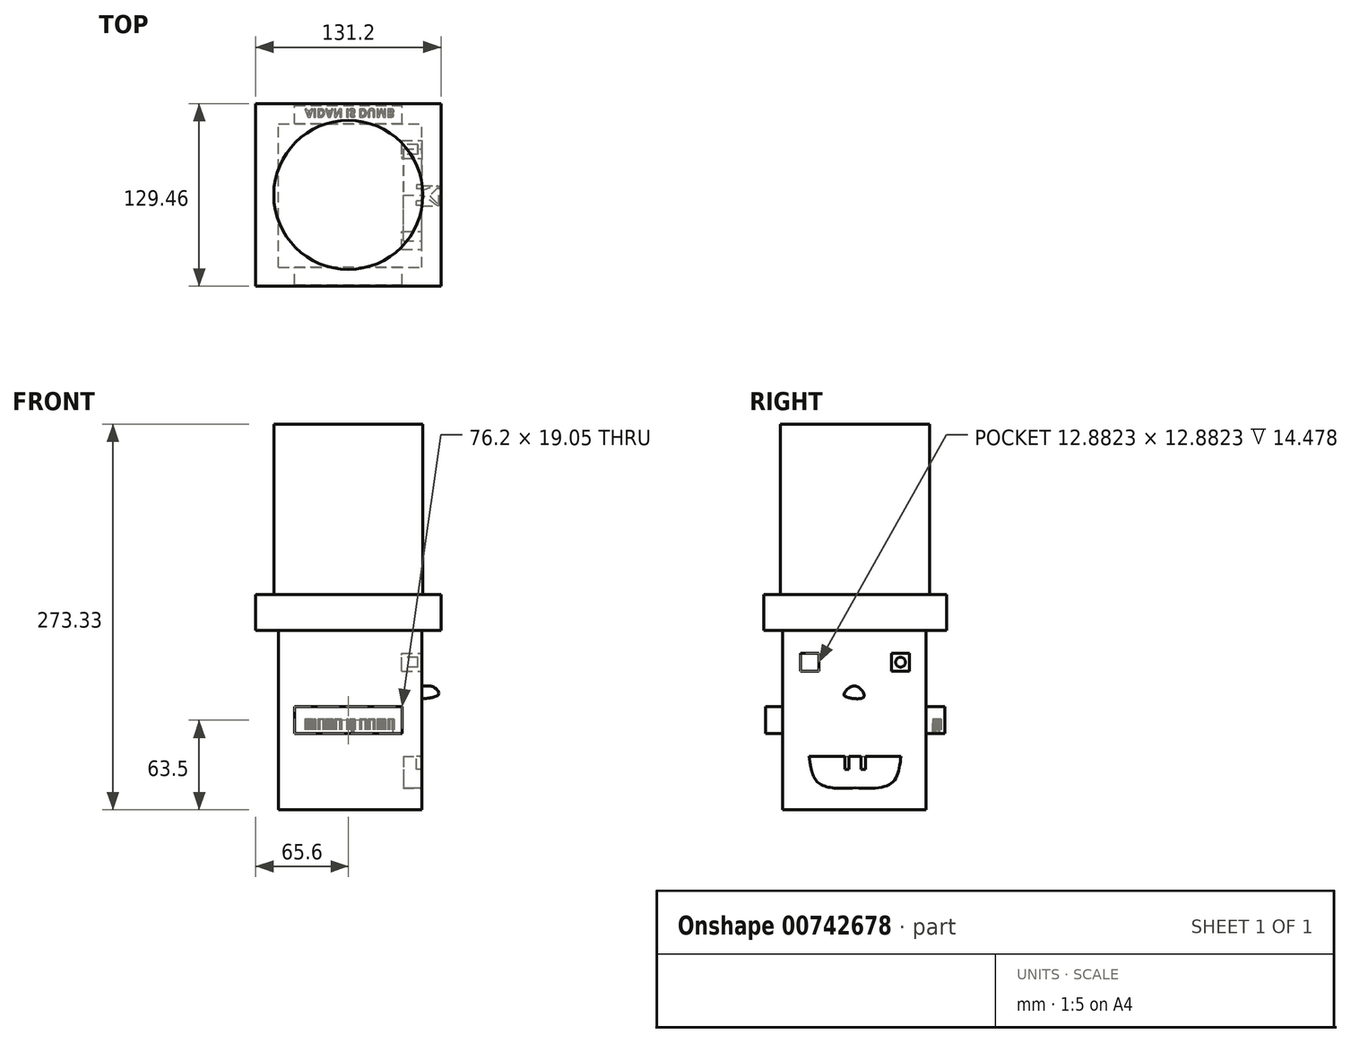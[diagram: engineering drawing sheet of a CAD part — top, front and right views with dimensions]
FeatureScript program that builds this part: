
annotation { "Feature Type Name" : "Feature", "Feature Type Description" : "" }
export const myFeature = defineFeature(function(context is Context, id is Id, definition is map)
    precondition{}
    {
        {
            var Q0;
            Q0=qCreatedBy(makeId("Front.planeOp"),FACE);
            var sketch = newSketch(context, id + "F0", { "sketchPlane" : qUnion([Q0])});
            skLineSegment(sketch, "E0.bottom", {"start": v(-38.1, -9.53) * mm, "end": v(38.1, -9.53) * mm});
            skLineSegment(sketch, "E0.top", {"start": v(-38.1, 9.53) * mm, "end": v(38.1, 9.53) * mm});
            skLineSegment(sketch, "E0.left", {"start": v(-38.1, -9.53) * mm, "end": v(-38.1, 9.53) * mm});
            skLineSegment(sketch, "E0.right", {"start": v(38.1, -9.53) * mm, "end": v(38.1, 9.53) * mm});
            skPoint(sketch, "E0.middle", {"position": v(0, 0) * mm});
            skLineSegment(sketch, "E1.bottom", {"start": v(69.87, 37.68) * mm, "end": v(98.1, 37.68) * mm});
            skLineSegment(sketch, "E1.top", {"start": v(69.87, 63.08) * mm, "end": v(98.1, 63.08) * mm});
            skLineSegment(sketch, "E1.left", {"start": v(69.87, 37.68) * mm, "end": v(69.87, 63.08) * mm});
            skLineSegment(sketch, "E1.right", {"start": v(98.1, 37.68) * mm, "end": v(98.1, 63.08) * mm});
            skPoint(sketch, "E1.middle", {"position": v(83.99, 50.38) * mm});
            skLineSegment(sketch, "E2", {"start": v(38.1, 9.52) * mm, "end": v(38.1, 38.1) * mm});
            skArc(sketch, "E3", {"start": v(38.1, 38.1) * mm, "mid": v(40.63, 43.9) * mm, "end": v(46.61, 45.99) * mm});
            skLineSegment(sketch, "E4", {"start": v(46.61, 45.99) * mm, "end": v(74.64, 45.99) * mm});
            skArc(sketch, "E5.0", {"start": v(28.2, 38.1) * mm, "mid": v(33.9, 51.17) * mm, "end": v(47.36, 55.87) * mm});
            skLineSegment(sketch, "E6", {"start": v(28.2, 38.1) * mm, "end": v(28.2, 9.52) * mm});
            skLineSegment(sketch, "E7", {"start": v(47.36, 55.87) * mm, "end": v(79, 55.87) * mm});
            skSolve(sketch);
        }
        {
            var Q0;
            Q0=makeQuery(id+"F0.imprint","IMPRINT",FACE,{"disambiguationData":[TD([[makeQuery(id+"F0.imprint","IMPRINT",EDGE,{"derivedFrom":sQuery(id+"F0.wireOp",EDGE,"E0.bottom")}),1.0]])]});
            extrude(context, id + "F1", {"entities" : qUnion([Q0]), "endBound" : BoundingType.SYMMETRIC, "depth" : 127 * mm, "offsetDistance" : 25.4 * mm});
        }
        {
            var Q0;
            Q0=qCreatedBy(makeId("Top.planeOp"),FACE);
            var sketch = newSketch(context, id + "F2", { "sketchPlane" : qUnion([Q0])});
            skLineSegment(sketch, "E8.bottom", {"start": v(-49.37, -51.34) * mm, "end": v(52.23, -51.34) * mm});
            skLineSegment(sketch, "E8.top", {"start": v(-49.37, 50.26) * mm, "end": v(52.23, 50.26) * mm});
            skLineSegment(sketch, "E8.left", {"start": v(-49.37, -51.34) * mm, "end": v(-49.37, 50.26) * mm});
            skLineSegment(sketch, "E8.right", {"start": v(52.23, -51.34) * mm, "end": v(52.23, 50.26) * mm});
            skSolve(sketch);
        }
        {
            var Q0;
            Q0=makeQuery(id+"F2.imprint","IMPRINT",FACE,{"disambiguationData":[TD([[makeQuery(id+"F2.imprint","IMPRINT",EDGE,{"derivedFrom":sQuery(id+"F2.wireOp",EDGE,"E8.bottom")}),1.0]])]});
            extrude(context, id + "F3", {"entities" : qUnion([Q0]), "operationType" : NewBodyOperationType.ADD, "endBound" : BoundingType.SYMMETRIC, "depth" : 127 * mm, "offsetDistance" : 25.4 * mm});
        }
        {
            var Q0;
            Q0=makeQuery(id+"F3.opExtrude","SWEPT_FACE",FACE,{"disambiguationData":[OSD([sQuery(id+"F2.wireOp",EDGE,"E8.right")])]});
            var sketch = newSketch(context, id + "F4", { "sketchPlane" : qUnion([Q0])});
            skLineSegment(sketch, "E9.bottom", {"start": v(-38.62, 34.67) * mm, "end": v(-25.74, 34.67) * mm});
            skLineSegment(sketch, "E9.top", {"start": v(-38.62, 47.55) * mm, "end": v(-25.74, 47.55) * mm});
            skLineSegment(sketch, "E9.left", {"start": v(-38.62, 34.67) * mm, "end": v(-38.62, 47.55) * mm});
            skLineSegment(sketch, "E9.right", {"start": v(-25.74, 34.67) * mm, "end": v(-25.74, 47.55) * mm});
            skPoint(sketch, "E9.middle", {"position": v(-32.18, 41.1) * mm});
            skPoint(sketch, "E10.MirrorP", {"position": v(32.18, 41.1) * mm});
            skLineSegment(sketch, "E11.MirrorCS", {"start": v(25.74, 34.67) * mm, "end": v(25.74, 47.55) * mm});
            skLineSegment(sketch, "E12.MirrorCS", {"start": v(38.62, 34.67) * mm, "end": v(25.74, 34.67) * mm});
            skLineSegment(sketch, "E13.MirrorCS", {"start": v(38.62, 34.67) * mm, "end": v(38.62, 47.55) * mm});
            skLineSegment(sketch, "E14.MirrorCS", {"start": v(38.62, 47.55) * mm, "end": v(25.74, 47.55) * mm});
            skSolve(sketch);
        }
        {
            var Q0;
            Q0 = qSketchRegion(id + "F4", true);
            extrude(context, id + "F5", {"entities" : qUnion([Q0]), "operationType" : NewBodyOperationType.REMOVE, "oppositeDirection" : true, "depth" : 14.48 * mm, "offsetDistance" : 25.4 * mm});
        }
        {
            var Q0;
            Q0=makeQuery(id+"F5.boolean.opBoolean","COPY",FACE,{"derivedFrom":makeQuery(id+"F5.opExtrude","CAP_FACE",FACE,{"disambiguationData":[OSD([sQuery(id+"F4.wireOp",EDGE,"E11.MirrorCS"),sQuery(id+"F4.wireOp",EDGE,"E12.MirrorCS"),sQuery(id+"F4.wireOp",EDGE,"E13.MirrorCS"),sQuery(id+"F4.wireOp",EDGE,"E14.MirrorCS")])],"isStart":false})});
            var sketch = newSketch(context, id + "F6", { "sketchPlane" : qUnion([Q0])});
            skCircle(sketch, "E15", {"center": v(32.18, 41.1) * mm, "radius": 3.5 * mm});
            skPoint(sketch, "E15.centerSnap0", {"position": v(32.18, 34.67) * mm});
            skPoint(sketch, "E15.centerSnap1", {"position": v(25.74, 41.1) * mm});
            skCircle(sketch, "E16.MirrorC", {"center": v(-32.18, 41.1) * mm, "radius": 3.5 * mm});
            skSolve(sketch);
        }
        {
            var Q0;
            Q0=makeQuery(id+"F6.imprint","IMPRINT",FACE,{"disambiguationData":[TD([[makeQuery(id+"F6.imprint","IMPRINT",EDGE,{"derivedFrom":sQuery(id+"F6.wireOp",EDGE,"E15")}),1.0]])]});
            var Q1;
            Q1=makeQuery(id+"F6.imprint","IMPRINT",FACE,{"disambiguationData":[TD([[makeQuery(id+"F6.imprint","IMPRINT",EDGE,{"derivedFrom":sQuery(id+"F6.wireOp",EDGE,"E16.MirrorC")}),-1.0]])]});
            extrude(context, id + "F7", {"entities" : qUnion([Q0, Q1]), "operationType" : NewBodyOperationType.ADD, "depth" : 11.43 * mm, "offsetDistance" : 25.4 * mm});
        }
        {
            var Q0;
            Q0=makeQuery(id+"F3.opExtrude","SWEPT_FACE",FACE,{"disambiguationData":[OSD([sQuery(id+"F2.wireOp",EDGE,"E8.right")])]});
            var sketch = newSketch(context, id + "F8", { "sketchPlane" : qUnion([Q0])});
            skFitSpline(sketch, "E17", {"points": [v(-32.56, -25.65) * mm, v(-25.87, -44.45) * mm, v(0, -47.95) * mm], "startDerivative": vector(6.38, -48.17) * mm, "endDerivative": vector(57.6, 2.43) * mm});
            skFitSpline(sketch, "E18", {"points": [v(-31.57, -33.14) * mm, v(-29.38, -39.75) * mm], "startDerivative": vector(2.13, -6.64) * mm, "endDerivative": vector(2.13, -6.64) * mm});
            skFitSpline(sketch, "E19.MirrorCS", {"points": [v(32.56, -25.65) * mm, v(25.87, -44.45) * mm, v(0, -47.95) * mm], "startDerivative": vector(-6.38, -48.17) * mm, "endDerivative": vector(-57.6, 2.43) * mm});
            skLineSegment(sketch, "E20", {"start": v(-32.56, -25.65) * mm, "end": v(32.56, -25.65) * mm});
            skSolve(sketch);
        }
        {
            var Q0;
            Q0 = qSketchRegion(id + "F8", true);
            extrude(context, id + "F9", {"entities" : qUnion([Q0]), "operationType" : NewBodyOperationType.REMOVE, "oppositeDirection" : true, "depth" : 13.2 * mm, "offsetDistance" : 25.4 * mm});
        }
        {
            var Q0;
            Q0=makeQuery(id+"F9.boolean.opBoolean","COPY",FACE,{"derivedFrom":makeQuery(id+"F9.opExtrude","SWEPT_FACE",FACE,{"disambiguationData":[OSD([sQuery(id+"F8.wireOp",EDGE,"E20")])]})});
            var sketch = newSketch(context, id + "F10", { "sketchPlane" : qUnion([Q0])});
            skLineSegment(sketch, "E21.bottom", {"start": v(52.23, -7.3) * mm, "end": v(48.24, -7.3) * mm});
            skLineSegment(sketch, "E21.top", {"start": v(52.23, -4.37) * mm, "end": v(48.24, -4.37) * mm});
            skLineSegment(sketch, "E21.left", {"start": v(52.23, -7.3) * mm, "end": v(52.23, -4.37) * mm});
            skLineSegment(sketch, "E21.right", {"start": v(48.24, -7.3) * mm, "end": v(48.24, -4.37) * mm});
            skLineSegment(sketch, "E22.MirrorCS", {"start": v(52.23, 4.37) * mm, "end": v(48.24, 4.37) * mm});
            skLineSegment(sketch, "E23.MirrorCS", {"start": v(52.23, 7.3) * mm, "end": v(48.24, 7.3) * mm});
            skLineSegment(sketch, "E24.MirrorCS", {"start": v(48.24, 7.3) * mm, "end": v(48.24, 4.37) * mm});
            skLineSegment(sketch, "E25.MirrorCS", {"start": v(52.23, 7.3) * mm, "end": v(52.23, 4.37) * mm});
            skSolve(sketch);
        }
        {
            var Q0;
            Q0=makeQuery(id+"F10.imprint","IMPRINT",FACE,{"disambiguationData":[TD([[makeQuery(id+"F10.imprint","IMPRINT",EDGE,{"derivedFrom":sQuery(id+"F10.wireOp",EDGE,"E23.MirrorCS")}),1.0]])]});
            var Q1;
            Q1=makeQuery(id+"F10.imprint","IMPRINT",FACE,{"disambiguationData":[TD([[makeQuery(id+"F10.imprint","IMPRINT",EDGE,{"derivedFrom":sQuery(id+"F10.wireOp",EDGE,"E21.bottom")}),-1.0]])]});
            extrude(context, id + "F11", {"entities" : qUnion([Q0, Q1]), "operationType" : NewBodyOperationType.ADD, "depth" : 9.16 * mm, "offsetDistance" : 25.4 * mm});
        }
        {
            var Q0;
            Q0=makeQuery(id+"F3.opExtrude","CAP_FACE",FACE,{"disambiguationData":[OSD([sQuery(id+"F2.wireOp",EDGE,"E8.bottom"),sQuery(id+"F2.wireOp",EDGE,"E8.top"),sQuery(id+"F2.wireOp",EDGE,"E8.left"),sQuery(id+"F2.wireOp",EDGE,"E8.right")])],"isStart":false});
            var sketch = newSketch(context, id + "F12", { "sketchPlane" : qUnion([Q0])});
            skLineSegment(sketch, "E26.bottom", {"start": v(65.6, -64.73) * mm, "end": v(-65.6, -64.73) * mm});
            skLineSegment(sketch, "E26.top", {"start": v(65.6, 64.73) * mm, "end": v(-65.6, 64.73) * mm});
            skLineSegment(sketch, "E26.left", {"start": v(65.6, -64.73) * mm, "end": v(65.6, 64.73) * mm});
            skLineSegment(sketch, "E26.right", {"start": v(-65.6, -64.73) * mm, "end": v(-65.6, 64.73) * mm});
            skPoint(sketch, "E26.middle", {"position": v(0, 0) * mm});
            skSolve(sketch);
        }
        {
            var Q0;
            Q0=makeQuery(id+"F12.imprint","IMPRINT",FACE,{"disambiguationData":[TD([[makeQuery(id+"F12.imprint","IMPRINT",EDGE,{"derivedFrom":sQuery(id+"F12.wireOp",EDGE,"E26.bottom")}),-1.0]])]});
            var Q1;
            Q1=makeQuery(id+"F12.imprint","IMPRINT",FACE,{"disambiguationData":[TD([[makeQuery(id+"F12.imprint","IMPRINT",EDGE,{"derivedFrom":makeQuery(id+"F3.opExtrude","CAP_EDGE",EDGE,{"disambiguationData":[OSD([sQuery(id+"F2.wireOp",EDGE,"E8.bottom")])],"isStart":false})}),1.0]])]});
            extrude(context, id + "F13", {"entities" : qUnion([Q0, Q1]), "operationType" : NewBodyOperationType.ADD, "depth" : 25.4 * mm, "offsetDistance" : 25.4 * mm});
        }
        {
            var Q0;
            Q0=makeQuery(id+"F13.opExtrude","CAP_FACE",FACE,{"disambiguationData":[OSD([sQuery(id+"F12.wireOp",EDGE,"E26.bottom"),sQuery(id+"F12.wireOp",EDGE,"E26.top"),sQuery(id+"F12.wireOp",EDGE,"E26.left"),sQuery(id+"F12.wireOp",EDGE,"E26.right")])],"isStart":false});
            var sketch = newSketch(context, id + "F14", { "sketchPlane" : qUnion([Q0])});
            skCircle(sketch, "E27", {"center": v(0, 0) * mm, "radius": 52.8 * mm});
            skSolve(sketch);
        }
        {
            var Q0;
            Q0=makeQuery(id+"F14.imprint","IMPRINT",FACE,{"disambiguationData":[TD([[makeQuery(id+"F14.imprint","IMPRINT",EDGE,{"derivedFrom":sQuery(id+"F14.wireOp",EDGE,"E27")}),1.0]])]});
            extrude(context, id + "F15", {"entities" : qUnion([Q0]), "operationType" : NewBodyOperationType.ADD, "depth" : 120.93 * mm, "offsetDistance" : 25.4 * mm});
        }
        {
            var Q0;
            Q0=makeQuery(id+"F11.boolean.opBoolean","MERGE",FACE,{"derivedFrom":[makeQuery(id+"F3.opExtrude","SWEPT_FACE",FACE,{"disambiguationData":[OSD([sQuery(id+"F2.wireOp",EDGE,"E8.right")])]}),makeQuery(id+"F11.opExtrude","SWEPT_FACE",FACE,{"disambiguationData":[OSD([sQuery(id+"F10.wireOp",EDGE,"E21.left")])]}),makeQuery(id+"F11.opExtrude","SWEPT_FACE",FACE,{"disambiguationData":[OSD([sQuery(id+"F10.wireOp",EDGE,"E25.MirrorCS")])]})]});
            var sketch = newSketch(context, id + "F16", { "sketchPlane" : qUnion([Q0])});
            skSolve(sketch);
        }
        {
            var Q0;
            {var subQ5=sQuery(id+"F2.wireOp",EDGE,"E8.right");Q0=makeQuery(id+"F16.imprint","IMPRINT",FACE,{"disambiguationData":[TD([[makeQuery(id+"F16.imprint","IMPRINT",EDGE,{"derivedFrom":makeQuery(id+"F3.opExtrude","CAP_EDGE",EDGE,{"disambiguationData":[OSD([subQ5])],"isStart":true})}),1.0]])]});}
            var sketch = newSketch(context, id + "F17", { "sketchPlane" : qUnion([Q0])});
            skFitSpline(sketch, "E28", {"points": [v(0, 24.19) * mm, v(-7.73, 18.73) * mm, v(-5.95, 16.4) * mm, v(6.2, 16.68) * mm, v(0, 24.19) * mm]});
            skSolve(sketch);
        }
        {
            var Q0;
            Q0 = qSketchRegion(id + "F17", true);
            extrude(context, id + "F18", {"entities" : qUnion([Q0]), "operationType" : NewBodyOperationType.ADD, "depth" : 11.94 * mm, "offsetDistance" : 25.4 * mm});
        }
        {
            var Q0;
            Q0=qCreatedBy(makeId("Front.planeOp"),FACE);
            var sketch = newSketch(context, id + "F19", { "sketchPlane" : qUnion([Q0])});
            skLineSegment(sketch, "E29", {"start": v(52.23, 24.22) * mm, "end": v(64.17, 24.22) * mm});
            skLineSegment(sketch, "E30", {"start": v(64.17, 15.2) * mm, "end": v(52.23, 15.2) * mm});
            skFitSpline(sketch, "E31", {"points": [v(52.23, 24.22) * mm, v(60.6, 23.34) * mm, v(63.93, 18.4) * mm, v(52.23, 15.2) * mm], "startDerivative": vector(26.83, 2.22) * mm, "endDerivative": vector(-41.53, -4.01) * mm});
            skLineSegment(sketch, "E32", {"start": v(52.23, 24.22) * mm, "end": v(52.23, 15.2) * mm});
            skLineSegment(sketch, "E33", {"start": v(52.23, 24.22) * mm, "end": v(52.23, 27) * mm});
            skLineSegment(sketch, "E34", {"start": v(52.23, 27) * mm, "end": v(68.37, 27) * mm});
            skLineSegment(sketch, "E35", {"start": v(68.37, 27) * mm, "end": v(68.37, 14.24) * mm});
            skLineSegment(sketch, "E36", {"start": v(68.37, 14.24) * mm, "end": v(52.23, 13.77) * mm});
            skLineSegment(sketch, "E37", {"start": v(52.23, 13.77) * mm, "end": v(52.23, 15.2) * mm});
            skSolve(sketch);
        }
        {
            var Q0;
            {var subQ0=sQuery(id+"F19.wireOp",EDGE,"E33");Q0=makeQuery(id+"F19.imprint","IMPRINT",FACE,{"disambiguationData":[TD([[makeQuery(id+"F19.imprint","IMPRINT",EDGE,{"derivedFrom":subQ0}),-1.0]])]});}
            extrude(context, id + "F20", {"entities" : qUnion([Q0]), "operationType" : NewBodyOperationType.REMOVE, "endBound" : BoundingType.SYMMETRIC, "depth" : 25.4 * mm, "offsetDistance" : 25.4 * mm});
        }
        {
            var Q0;
            {var subQ2=sQuery(id+"F0.wireOp",EDGE,"E0.bottom");Q0=makeQuery(id+"F3.boolean.opBoolean","SPLIT",FACE,{"disambiguationData":[TD([makeQuery(id+"F3.opExtrude","SWEPT_FACE",FACE,{"disambiguationData":[OSD([sQuery(id+"F2.wireOp",EDGE,"E8.top")])]})])],"derivedFrom":makeQuery(id+"F1.opExtrude","SWEPT_FACE",FACE,{"disambiguationData":[OSD([subQ2])]})});}
            var sketch = newSketch(context, id + "F21", { "sketchPlane" : qUnion([Q0])});
            skText(sketch, "E38", { "text": "AIDAN IS DUMB\n", "fontName": "OpenSans-Bold.ttf"});
            const initialGuessF21  = {"E38": [-0.0307, -0.06096, 1, 0, 0.00587]};
            skSetInitialGuess(sketch, initialGuessF21);
            skSolve(sketch);
        }
        {
            var Q0;
            Q0 = qSketchRegion(id + "F21", true);
            extrude(context, id + "F22", {"entities" : qUnion([Q0]), "operationType" : NewBodyOperationType.REMOVE, "oppositeDirection" : true, "depth" : 10.16 * mm, "offsetDistance" : 25.4 * mm});
        }
    });
